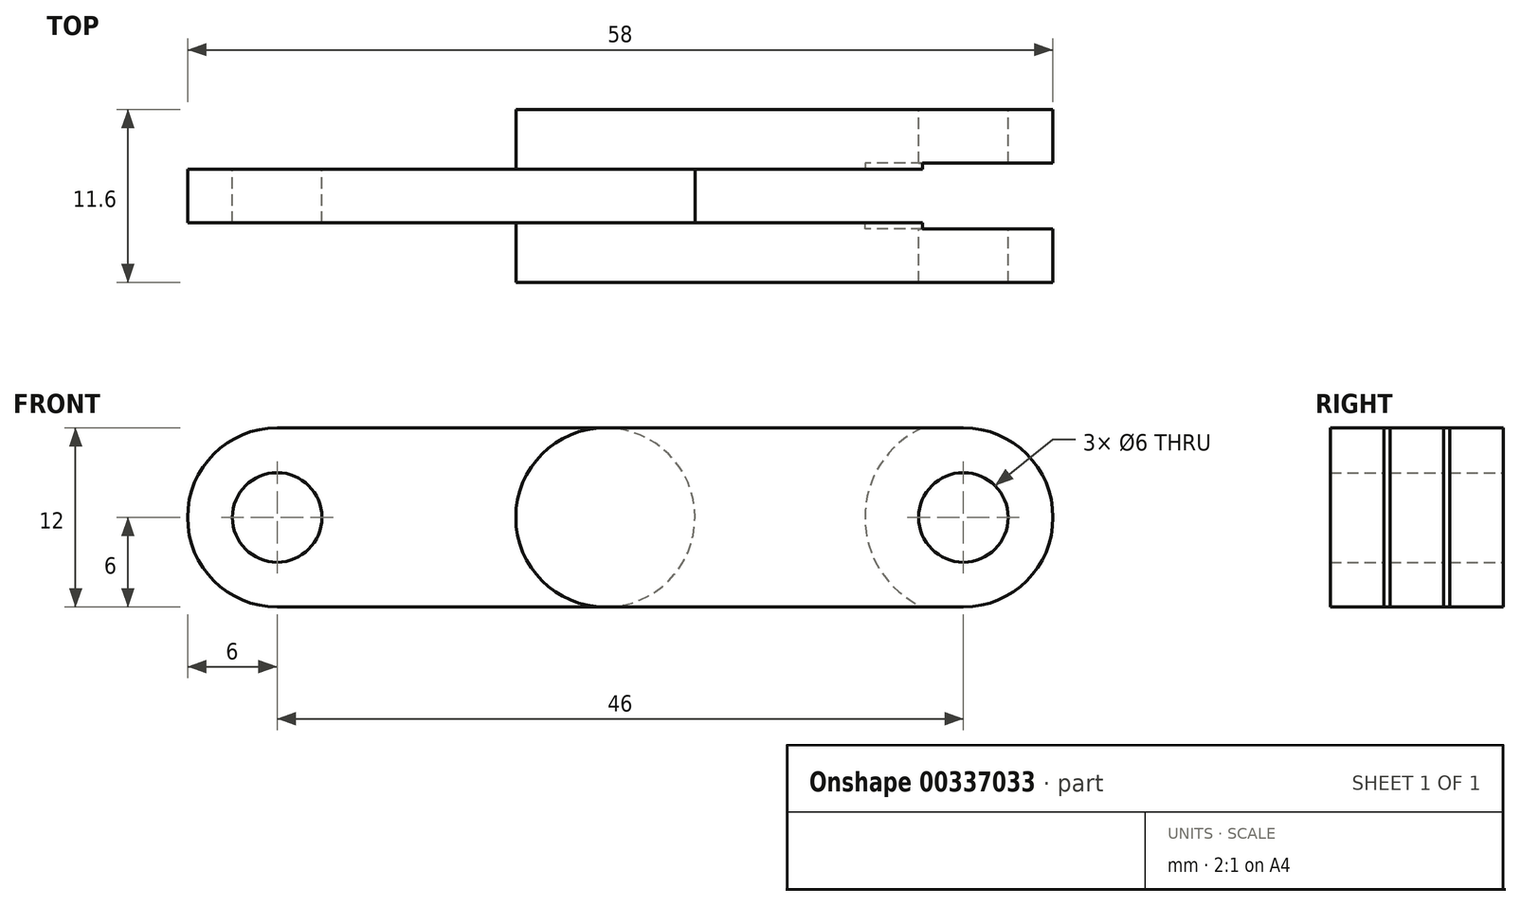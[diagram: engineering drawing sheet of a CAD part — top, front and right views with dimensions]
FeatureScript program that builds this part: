
annotation { "Feature Type Name" : "Feature", "Feature Type Description" : "" }
export const myFeature = defineFeature(function(context is Context, id is Id, definition is map)
    precondition{}
    {
        {
            var Q0;
            Q0=qCreatedBy(makeId("Front.planeOp"),FACE);
            var sketch = newSketch(context, id + "F0", { "sketchPlane" : qUnion([Q0])});
            skLineSegment(sketch, "E0", {"start": v(0, 12) * mm, "end": v(22, 12) * mm});
            skLineSegment(sketch, "E1", {"start": v(0, 0) * mm, "end": v(22, 0) * mm});
            skLineSegment(sketch, "E2", {"start": v(0, 12) * mm, "end": v(0, 0) * mm, "construction": true});
            skLineSegment(sketch, "E3", {"start": v(22, 12) * mm, "end": v(22, 0) * mm, "construction": true});
            skArc(sketch, "E4", {"start": v(0, 12) * mm, "mid": v(-6, 6) * mm, "end": v(0, 0) * mm});
            skArc(sketch, "E5", {"start": v(22, 12) * mm, "mid": v(28, 6) * mm, "end": v(22, 0) * mm});
            skCircle(sketch, "E6", {"center": v(0, 6) * mm, "radius": 3 * mm});
            skSolve(sketch);
        }
        {
            var Q0;
            Q0=makeQuery(id+"F0.imprint","IMPRINT",FACE,{"disambiguationData":[TD([[makeQuery(id+"F0.imprint","IMPRINT",EDGE,{"derivedFrom":sQuery(id+"F0.wireOp",EDGE,"E0")}),-1.0]])]});
            extrude(context, id + "F1", {"entities" : qUnion([Q0]), "depth" : 3.6 * mm});
        }
        {
            var Q0;
            Q0=qCreatedBy(makeId("Front.planeOp"),FACE);
            var sketch = newSketch(context, id + "F2", { "sketchPlane" : qUnion([Q0])});
            skLineSegment(sketch, "E7", {"start": v(22, 12) * mm, "end": v(46, 12) * mm});
            skLineSegment(sketch, "E8", {"start": v(22, 0) * mm, "end": v(46, 0) * mm});
            skLineSegment(sketch, "E9", {"start": v(46, 12) * mm, "end": v(46, 0) * mm, "construction": true});
            skLineSegment(sketch, "E10", {"start": v(22, 12) * mm, "end": v(22, 0) * mm, "construction": true});
            skArc(sketch, "E11", {"start": v(46, 12) * mm, "mid": v(52, 6) * mm, "end": v(46, 0) * mm});
            skArc(sketch, "E12", {"start": v(22, 12) * mm, "mid": v(16, 6) * mm, "end": v(22, 0) * mm});
            skSolve(sketch);
        }
        {
            var Q0;
            Q0=qSketchRegion(id+"F2",true);
            extrude(context, id + "F3", {"entities" : qUnion([Q0]), "operationType" : NewBodyOperationType.ADD, "oppositeDirection" : true, "depth" : 4 * mm});
        }
        {
            var Q0;
            Q0=makeQuery(id+"F1.opExtrude","CAP_FACE",FACE,{"disambiguationData":[OSD([sQuery(id+"F0.wireOp",EDGE,"E0"),sQuery(id+"F0.wireOp",EDGE,"E1"),sQuery(id+"F0.wireOp",EDGE,"E4"),sQuery(id+"F0.wireOp",EDGE,"E5"),sQuery(id+"F0.wireOp",EDGE,"E6")])],"isStart":false});
            var sketch = newSketch(context, id + "F4", { "sketchPlane" : qUnion([Q0])});
            skLineSegment(sketch, "E13", {"start": v(22, 12) * mm, "end": v(46, 12) * mm});
            skLineSegment(sketch, "E14", {"start": v(46, 12) * mm, "end": v(46, 0) * mm, "construction": true});
            skLineSegment(sketch, "E15", {"start": v(46, 0) * mm, "end": v(22, 0) * mm});
            skLineSegment(sketch, "E16", {"start": v(22, 0) * mm, "end": v(22, 12) * mm, "construction": true});
            skArc(sketch, "E17", {"start": v(22, 12) * mm, "mid": v(16, 6) * mm, "end": v(22, 0) * mm});
            skArc(sketch, "E18", {"start": v(46, 12) * mm, "mid": v(52, 6) * mm, "end": v(46, 0) * mm});
            skSolve(sketch);
        }
        {
            var Q0;
            Q0=qSketchRegion(id+"F4",true);
            extrude(context, id + "F5", {"entities" : qUnion([Q0]), "operationType" : NewBodyOperationType.ADD, "depth" : 4 * mm});
        }
        {
            var Q0;
            Q0=makeQuery(id+"F2.imprint","IMPRINT",FACE,{"disambiguationData":[TD([[makeQuery(id+"F2.imprint","IMPRINT",EDGE,{"derivedFrom":sQuery(id+"F2.wireOp",EDGE,"E7")}),-1.0]])]});
            var sketch = newSketch(context, id + "F6", { "sketchPlane" : qUnion([Q0])});
            skCircle(sketch, "E19", {"center": v(46, 6) * mm, "radius": 3 * mm});
            skSolve(sketch);
        }
        {
            var Q0;
            Q0=makeQuery(id+"F5.opExtrude","CAP_FACE",FACE,{"disambiguationData":[OSD([sQuery(id+"F4.wireOp",EDGE,"E13"),sQuery(id+"F4.wireOp",EDGE,"E15"),sQuery(id+"F4.wireOp",EDGE,"E17"),sQuery(id+"F4.wireOp",EDGE,"E18")])],"isStart":true});
            var sketch = newSketch(context, id + "F7", { "sketchPlane" : qUnion([Q0])});
            skCircle(sketch, "E20", {"center": v(-46, 6) * mm, "radius": 6.6 * mm});
            skSolve(sketch);
        }
        {
            var Q0;
            Q0=makeQuery(id+"F2.imprint","IMPRINT",FACE,{"disambiguationData":[TD([[makeQuery(id+"F2.imprint","IMPRINT",EDGE,{"derivedFrom":sQuery(id+"F2.wireOp",EDGE,"E7")}),-1.0]])]});
            var sketch = newSketch(context, id + "F8", { "sketchPlane" : qUnion([Q0])});
            skCircle(sketch, "E21", {"center": v(46, 6) * mm, "radius": 6.6 * mm});
            skSolve(sketch);
        }
        {
            var Q0;
            Q0 = qSketchRegion(id + "F7", true);
            extrude(context, id + "F9", {"entities" : qUnion([Q0]), "operationType" : NewBodyOperationType.REMOVE, "oppositeDirection" : true, "depth" : 0.4 * mm});
        }
        {
            var Q0;
            Q0 = qSketchRegion(id + "F8", true);
            extrude(context, id + "F10", {"entities" : qUnion([Q0]), "operationType" : NewBodyOperationType.REMOVE, "oppositeDirection" : true, "depth" : 0.4 * mm});
        }
        {
            var Q0;
            Q0=qSketchRegion(id+"F6",true);
            extrude(context, id + "F11", {"entities" : qUnion([Q0]), "operationType" : NewBodyOperationType.REMOVE, "endBound" : BoundingType.THROUGH_ALL, "depth" : 25 * mm, "hasSecondDirection" : true, "secondDirectionBound" : SecondDirectionBoundingType.THROUGH_ALL, "secondDirectionOppositeDirection" : true, "secondDirectionDepth" : 25 * mm});
        }
    });
